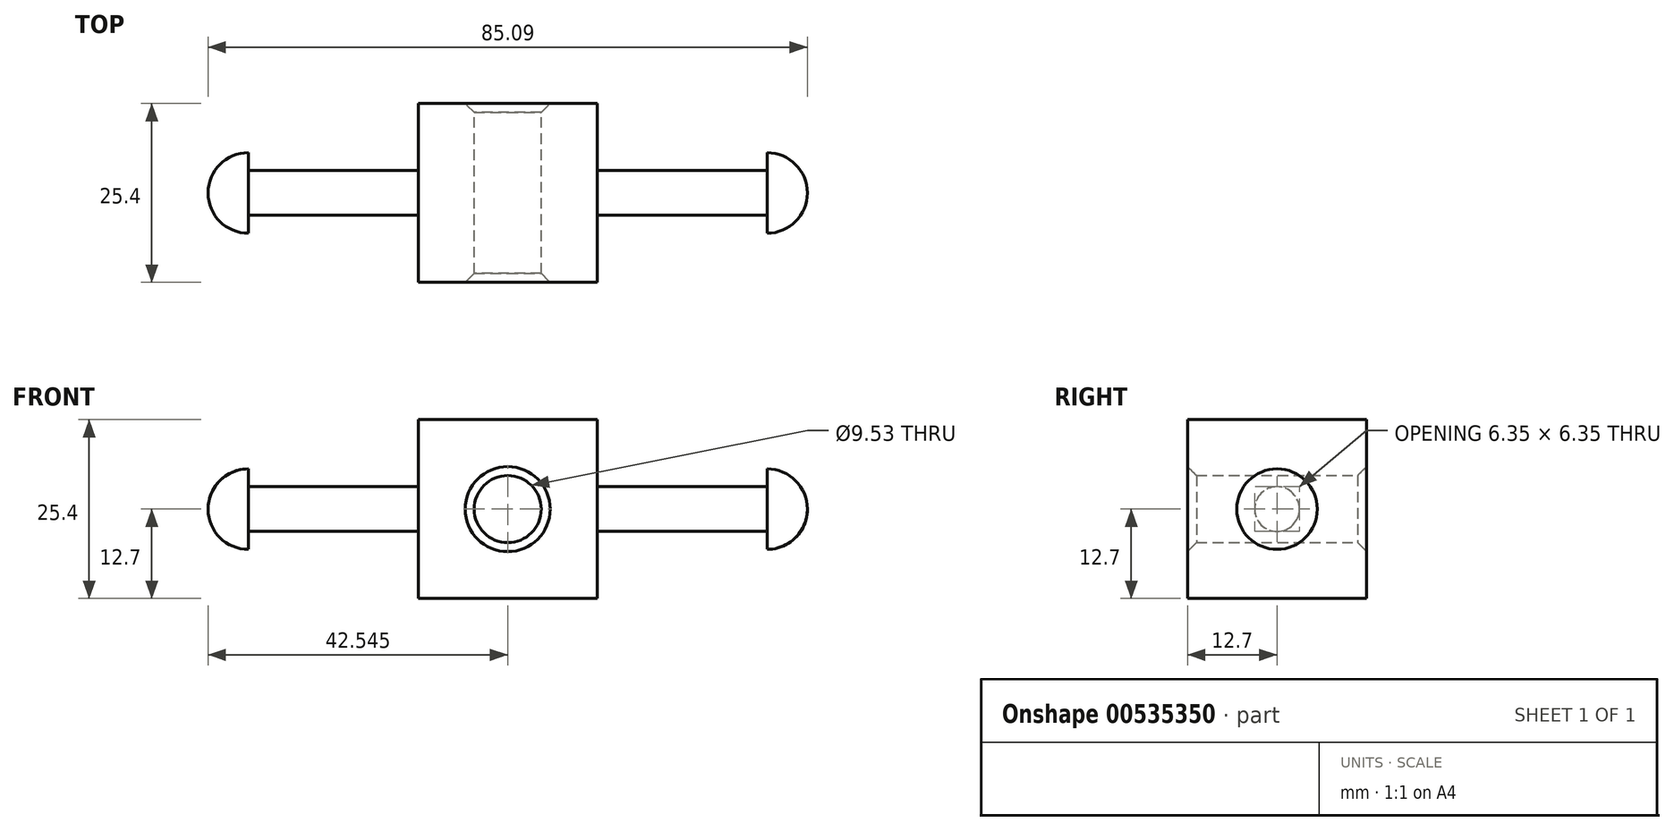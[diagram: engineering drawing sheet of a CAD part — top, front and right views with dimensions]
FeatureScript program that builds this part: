
annotation { "Feature Type Name" : "Feature", "Feature Type Description" : "" }
export const myFeature = defineFeature(function(context is Context, id is Id, definition is map)
    precondition{}
    {
        {
            var Q0;
            Q0=qCreatedBy(makeId("Front.planeOp"),FACE);
            var sketch = newSketch(context, id + "F0", { "sketchPlane" : qUnion([Q0])});
            skLineSegment(sketch, "E0", {"start": v(-79.38, 5.71) * mm, "end": v(-79.38, 3.18) * mm});
            skLineSegment(sketch, "E1", {"start": v(-79.38, 3.17) * mm, "end": v(-5.71, 3.17) * mm});
            skLineSegment(sketch, "E2", {"start": v(-5.72, 3.17) * mm, "end": v(-5.72, 5.72) * mm});
            skLineSegment(sketch, "E3", {"start": v(0, 0) * mm, "end": v(-85.1, 0) * mm});
            skArc(sketch, "E4", {"start": v(0, 0) * mm, "mid": v(-1.67, 4.04) * mm, "end": v(-5.72, 5.72) * mm});
            skArc(sketch, "E5", {"start": v(-79.38, 5.71) * mm, "mid": v(-83.42, 4.04) * mm, "end": v(-85.1, 0) * mm});
            skLineSegment(sketch, "E6", {"start": v(0, 0) * mm, "end": v(16.7, 0) * mm, "construction": true});
            skSolve(sketch);
        }
        {
            var Q0;
            Q0=makeQuery(id+"F0.imprint","IMPRINT",FACE,{"disambiguationData":[TD([[makeQuery(id+"F0.imprint","IMPRINT",EDGE,{"derivedFrom":sQuery(id+"F0.wireOp",EDGE,"E0")}),-1.0]])]});
            var Q1;
            Q1=sQuery(id+"F0.wireOp",EDGE,"E6");
            revolve(context, id + "F1", {"entities" : qUnion([Q0]), "axis" : qUnion([Q1]), "revolveType" : RevolveType.FULL});
        }
        {
            var Q0;
            Q0=qCreatedBy(makeId("Front.planeOp"),FACE);
            var sketch = newSketch(context, id + "F2", { "sketchPlane" : qUnion([Q0])});
            skLineSegment(sketch, "E7.bottom", {"start": v(-55.24, 12.7) * mm, "end": v(-29.85, 12.7) * mm});
            skLineSegment(sketch, "E7.top", {"start": v(-55.24, -12.7) * mm, "end": v(-29.85, -12.7) * mm});
            skLineSegment(sketch, "E7.left", {"start": v(-55.24, 12.7) * mm, "end": v(-55.24, -12.7) * mm});
            skLineSegment(sketch, "E7.right", {"start": v(-29.84, 12.7) * mm, "end": v(-29.84, -12.7) * mm});
            skLineSegment(sketch, "E8", {"start": v(-55.24, 0) * mm, "end": v(-29.85, 0) * mm, "construction": true});
            skPoint(sketch, "E9", {"position": v(-42.55, 0) * mm});
            skLineSegment(sketch, "E10.0", {"start": v(0, 0) * mm, "end": v(-85.1, 0) * mm, "construction": true});
            skSolve(sketch);
        }
        {
            var Q0;
            Q0 = qSketchRegion(id + "F2", true);
            extrude(context, id + "F3", {"entities" : qUnion([Q0]), "operationType" : NewBodyOperationType.ADD, "endBound" : BoundingType.SYMMETRIC, "depth" : 25.4 * mm, "offsetDistance" : 25.4 * mm});
        }
        {
            var Q0;
            Q0=qCreatedBy(makeId("Right.planeOp"),FACE);
            var Q1;
            Q1=sQuery(id+"F2.wireOp",VERTEX,"E9");
            cPlane(context, id + "F4", {"entities" : qUnion([Q0, Q1]), "cplaneType" : CPlaneType.PLANE_POINT, "offset" : 25.4 * mm, "width" : 152.4 * mm, "height" : 152.4 * mm});
        }
        {
            var Q0;
            Q0=qCreatedBy(id+"F4.planeOp",FACE);
            var sketch = newSketch(context, id + "F5", { "sketchPlane" : qUnion([Q0])});
            skLineSegment(sketch, "E11", {"start": v(-12.7, 0) * mm, "end": v(12.7, 0) * mm});
            skLineSegment(sketch, "E12.0.0", {"start": v(12.7, -12.7) * mm, "end": v(12.7, 12.7) * mm, "construction": true});
            skLineSegment(sketch, "E12.0.1", {"start": v(12.7, 12.7) * mm, "end": v(-12.7, 12.7) * mm, "construction": true});
            skLineSegment(sketch, "E12.0.2", {"start": v(-12.7, 12.7) * mm, "end": v(-12.7, -12.7) * mm, "construction": true});
            skLineSegment(sketch, "E12.0.3", {"start": v(-12.7, -12.7) * mm, "end": v(12.7, -12.7) * mm, "construction": true});
            skLineSegment(sketch, "E13", {"start": v(-12.7, 0) * mm, "end": v(-12.7, 6.03) * mm});
            skLineSegment(sketch, "E14", {"start": v(-12.7, 6.03) * mm, "end": v(-11.43, 4.76) * mm});
            skLineSegment(sketch, "E15", {"start": v(-11.43, 4.76) * mm, "end": v(11.43, 4.76) * mm});
            skLineSegment(sketch, "E16", {"start": v(12.7, 0) * mm, "end": v(32.92, 0) * mm, "construction": true});
            skLineSegment(sketch, "E17", {"start": v(12.7, 0) * mm, "end": v(12.7, 6.03) * mm});
            skLineSegment(sketch, "E18", {"start": v(12.7, 6.03) * mm, "end": v(11.43, 4.76) * mm});
            skLineSegment(sketch, "E19", {"start": v(-12.7, 6.03) * mm, "end": v(12.7, 6.03) * mm, "construction": true});
            skSolve(sketch);
        }
        {
            var Q0;
            Q0 = qSketchRegion(id + "F5", true);
            var Q1;
            Q1=sQuery(id+"F5.wireOp",EDGE,"E16");
            revolve(context, id + "F6", {"operationType" : NewBodyOperationType.REMOVE, "entities" : qUnion([Q0]), "axis" : qUnion([Q1]), "revolveType" : RevolveType.FULL, "oppositeDirection" : true});
        }
    });
